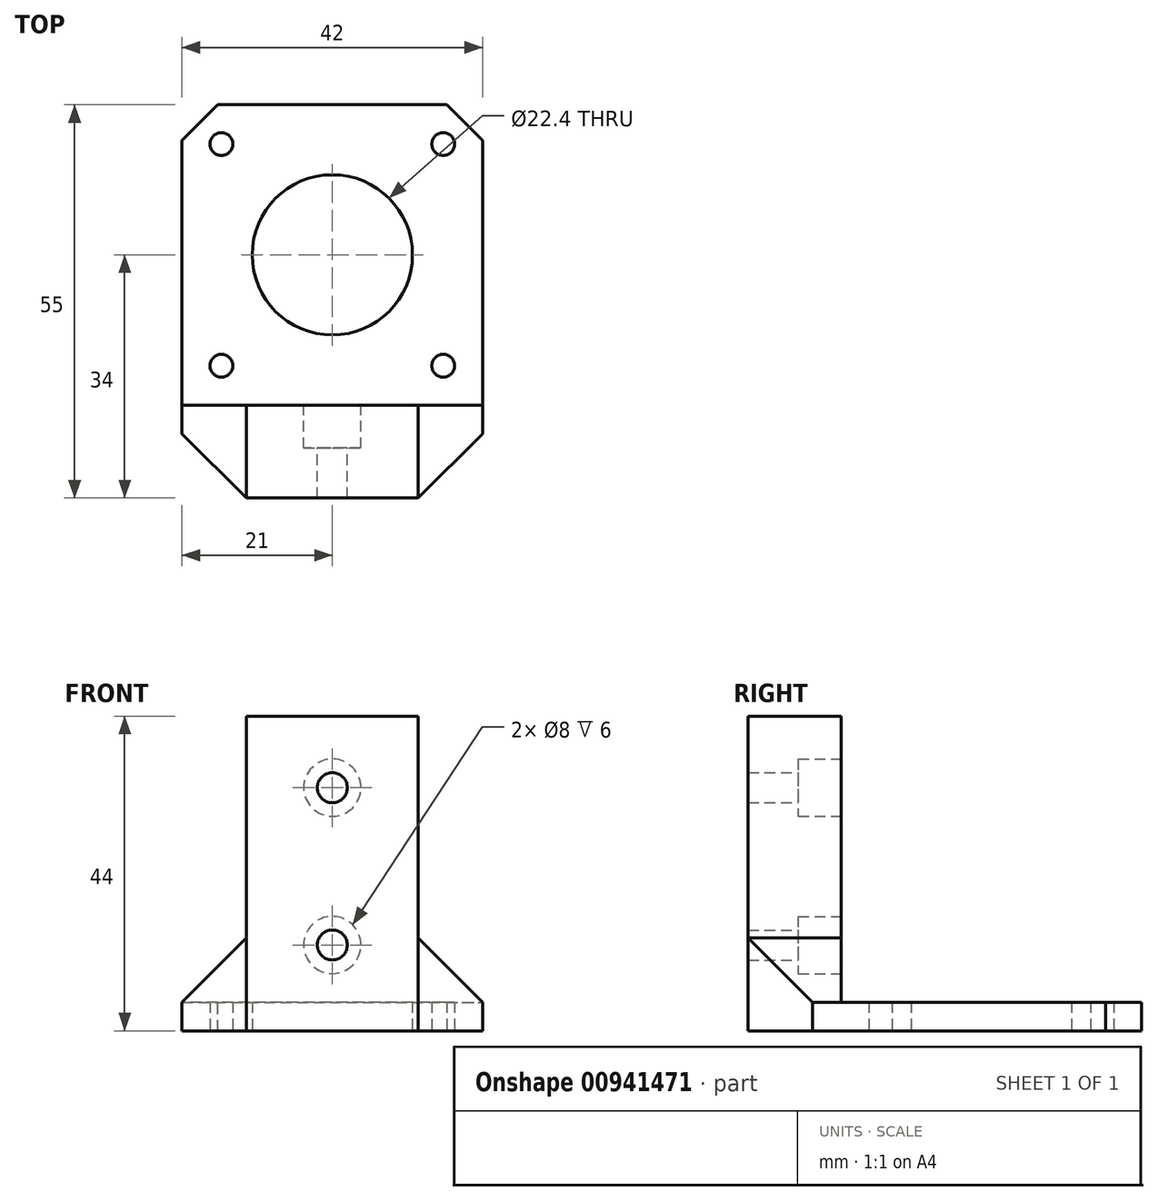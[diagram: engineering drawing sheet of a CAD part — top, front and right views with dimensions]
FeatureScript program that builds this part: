
annotation { "Feature Type Name" : "Feature", "Feature Type Description" : "" }
export const myFeature = defineFeature(function(context is Context, id is Id, definition is map)
    precondition{}
    {
        {
            var Q0;
            Q0=qCreatedBy(makeId("Top.planeOp"),FACE);
            var sketch = newSketch(context, id + "F0", { "sketchPlane" : qUnion([Q0])});
            skLineSegment(sketch, "E0.bottom", {"start": v(21, -21) * mm, "end": v(-21, -21) * mm});
            skLineSegment(sketch, "E0.top", {"start": v(21, 21) * mm, "end": v(-21, 21) * mm});
            skLineSegment(sketch, "E0.left", {"start": v(21, -21) * mm, "end": v(21, 21) * mm});
            skLineSegment(sketch, "E0.right", {"start": v(-21, -21) * mm, "end": v(-21, 21) * mm});
            skPoint(sketch, "E0.middle", {"position": v(0, 0) * mm});
            skLineSegment(sketch, "E1.bottom", {"start": v(-12, -21) * mm, "end": v(12, -21) * mm});
            skLineSegment(sketch, "E1.top", {"start": v(-12, -34) * mm, "end": v(12, -34) * mm});
            skLineSegment(sketch, "E1.left", {"start": v(-12, -21) * mm, "end": v(-12, -34) * mm});
            skLineSegment(sketch, "E1.right", {"start": v(12, -21) * mm, "end": v(12, -34) * mm});
            skCircle(sketch, "E2", {"center": v(0, 0) * mm, "radius": 11.2 * mm});
            skCircle(sketch, "E3", {"center": v(-15.5, 15.5) * mm, "radius": 1.6 * mm});
            skCircle(sketch, "E4", {"center": v(15.5, 15.5) * mm, "radius": 1.6 * mm});
            skCircle(sketch, "E5", {"center": v(15.5, -15.5) * mm, "radius": 1.6 * mm});
            skCircle(sketch, "E6", {"center": v(-15.5, -15.5) * mm, "radius": 1.6 * mm});
            skSolve(sketch);
        }
        {
            var Q0;
            Q0=makeQuery(id+"F0.imprint","IMPRINT",FACE,{"disambiguationData":[TD([[makeQuery(id+"F0.imprint","IMPRINT",EDGE,{"derivedFrom":sQuery(id+"F0.wireOp",EDGE,"E0.top")}),1.0]])]});
            var Q1;
            Q1=makeQuery(id+"F0.imprint","IMPRINT",FACE,{"disambiguationData":[TD([[makeQuery(id+"F0.imprint","IMPRINT",EDGE,{"derivedFrom":sQuery(id+"F0.wireOp",EDGE,"E1.top")}),1.0]])]});
            extrude(context, id + "F1", {"entities" : qUnion([Q0, Q1]), "depth" : 4 * mm, "offsetDistance" : 25 * mm});
        }
        {
            var Q0;
            Q0=makeQuery(id+"F1.opExtrude","CAP_FACE",FACE,{"disambiguationData":[OSD([sQuery(id+"F0.wireOp",EDGE,"E0.bottom"),sQuery(id+"F0.wireOp",EDGE,"E0.top"),sQuery(id+"F0.wireOp",EDGE,"E0.left"),sQuery(id+"F0.wireOp",EDGE,"E0.right"),sQuery(id+"F0.wireOp",EDGE,"E1.top"),sQuery(id+"F0.wireOp",EDGE,"E1.left"),sQuery(id+"F0.wireOp",EDGE,"E1.right"),sQuery(id+"F0.wireOp",EDGE,"E2"),sQuery(id+"F0.wireOp",EDGE,"E3"),sQuery(id+"F0.wireOp",EDGE,"E4"),sQuery(id+"F0.wireOp",EDGE,"E5"),sQuery(id+"F0.wireOp",EDGE,"E6")])],"isStart":false});
            var sketch = newSketch(context, id + "F2", { "sketchPlane" : qUnion([Q0])});
            skLineSegment(sketch, "E7.bottom", {"start": v(-12, -34) * mm, "end": v(12, -34) * mm});
            skLineSegment(sketch, "E7.top", {"start": v(-12, -21) * mm, "end": v(12, -21) * mm});
            skLineSegment(sketch, "E7.left", {"start": v(-12, -34) * mm, "end": v(-12, -21) * mm});
            skLineSegment(sketch, "E7.right", {"start": v(12, -34) * mm, "end": v(12, -21) * mm});
            skSolve(sketch);
        }
        {
            var Q0;
            Q0=makeQuery(id+"F2.imprint","IMPRINT",FACE,{"disambiguationData":[TD([[makeQuery(id+"F2.imprint","IMPRINT",EDGE,{"derivedFrom":sQuery(id+"F2.wireOp",EDGE,"E7.bottom")}),1.0]])]});
            extrude(context, id + "F3", {"entities" : qUnion([Q0]), "operationType" : NewBodyOperationType.ADD, "depth" : 40 * mm, "offsetDistance" : 25 * mm});
        }
        {
            var Q0;
            Q0=makeQuery(id+"F1.opExtrude","SWEPT_EDGE",EDGE,{"disambiguationData":[OSD([sQuery(id+"F0.wireOp",EDGE,"E0.bottom"),sQuery(id+"F0.wireOp",EDGE,"E1.right")])]});
            var Q1;
            Q1=makeQuery(id+"F1.opExtrude","SWEPT_EDGE",EDGE,{"disambiguationData":[OSD([sQuery(id+"F0.wireOp",EDGE,"E0.bottom"),sQuery(id+"F0.wireOp",EDGE,"E1.left")])]});
            chamfer(context, id + "F4", {"entities" : qUnion([Q0, Q1]), "width" : 13 * mm, "tangentPropagation" : true});
        }
        {
            var Q0;
            {var subQ0=sQuery(id+"F0.wireOp",EDGE,"E0.bottom");Q0=makeQuery(id+"F4.opChamfer","TWEAK_EDGE",EDGE,{"derivedFrom":[makeQuery(id+"F3.boolean.opBoolean","MERGE",VERTEX,{"derivedFrom":[makeQuery(id+"F1.opExtrude","CAP_VERTEX",VERTEX,{"disambiguationData":[OSD([subQ0,sQuery(id+"F0.wireOp",EDGE,"E1.right")])],"isStart":false}),makeQuery(id+"F3.opExtrude","CAP_VERTEX",VERTEX,{"disambiguationData":[OSD([subQ0,sQuery(id+"F2.wireOp",EDGE,"E7.top"),sQuery(id+"F2.wireOp",EDGE,"E7.right")])],"isStart":true})]})]});}
            var Q1;
            {var subQ0=sQuery(id+"F0.wireOp",EDGE,"E0.bottom");Q1=makeQuery(id+"F4.opChamfer","TWEAK_EDGE",EDGE,{"derivedFrom":[makeQuery(id+"F3.boolean.opBoolean","MERGE",VERTEX,{"derivedFrom":[makeQuery(id+"F1.opExtrude","CAP_VERTEX",VERTEX,{"disambiguationData":[OSD([subQ0,sQuery(id+"F0.wireOp",EDGE,"E1.left")])],"isStart":false}),makeQuery(id+"F3.opExtrude","CAP_VERTEX",VERTEX,{"disambiguationData":[OSD([subQ0,sQuery(id+"F2.wireOp",EDGE,"E7.top"),sQuery(id+"F2.wireOp",EDGE,"E7.left")])],"isStart":true})]})]});}
            chamfer(context, id + "F5", {"entities" : qUnion([Q0, Q1]), "width" : 9 * mm, "tangentPropagation" : true});
        }
        {
            var Q0;
            Q0=makeQuery(id+"F3.opExtrude","SWEPT_FACE",FACE,{"disambiguationData":[OSD([sQuery(id+"F2.wireOp",EDGE,"E7.top")])]});
            var sketch = newSketch(context, id + "F6", { "sketchPlane" : qUnion([Q0])});
            skCircle(sketch, "E8", {"center": v(0, 34) * mm, "radius": 2.1 * mm});
            skCircle(sketch, "E9", {"center": v(0, 12) * mm, "radius": 2.1 * mm});
            skCircle(sketch, "E10", {"center": v(0, 34) * mm, "radius": 4 * mm});
            skCircle(sketch, "E11", {"center": v(0, 12) * mm, "radius": 4 * mm});
            skSolve(sketch);
        }
        {
            var Q0;
            Q0=makeQuery(id+"F6.imprint","IMPRINT",FACE,{"disambiguationData":[TD([[makeQuery(id+"F6.imprint","IMPRINT",EDGE,{"derivedFrom":sQuery(id+"F6.wireOp",EDGE,"E8")}),1.0]])]});
            var Q1;
            Q1=makeQuery(id+"F6.imprint","IMPRINT",FACE,{"disambiguationData":[TD([[makeQuery(id+"F6.imprint","IMPRINT",EDGE,{"derivedFrom":sQuery(id+"F6.wireOp",EDGE,"E9")}),1.0]])]});
            extrude(context, id + "F7", {"entities" : qUnion([Q0, Q1]), "operationType" : NewBodyOperationType.REMOVE, "oppositeDirection" : true, "depth" : 25 * mm, "offsetDistance" : 25 * mm});
        }
        {
            var Q0;
            Q0=makeQuery(id+"F6.imprint","IMPRINT",FACE,{"disambiguationData":[TD([[makeQuery(id+"F6.imprint","IMPRINT",EDGE,{"derivedFrom":sQuery(id+"F6.wireOp",EDGE,"E8")}),-1.0]])]});
            var Q1;
            Q1=makeQuery(id+"F6.imprint","IMPRINT",FACE,{"disambiguationData":[TD([[makeQuery(id+"F6.imprint","IMPRINT",EDGE,{"derivedFrom":sQuery(id+"F6.wireOp",EDGE,"E9")}),-1.0]])]});
            extrude(context, id + "F8", {"entities" : qUnion([Q0, Q1]), "operationType" : NewBodyOperationType.REMOVE, "oppositeDirection" : true, "depth" : 6 * mm, "offsetDistance" : 25 * mm});
        }
        {
            var Q0;
            Q0=makeQuery(id+"F1.opExtrude","SWEPT_EDGE",EDGE,{"disambiguationData":[OSD([sQuery(id+"F0.wireOp",EDGE,"E0.top"),sQuery(id+"F0.wireOp",EDGE,"E0.left")])]});
            var Q1;
            Q1=makeQuery(id+"F1.opExtrude","SWEPT_EDGE",EDGE,{"disambiguationData":[OSD([sQuery(id+"F0.wireOp",EDGE,"E0.top"),sQuery(id+"F0.wireOp",EDGE,"E0.right")])]});
            chamfer(context, id + "F9", {"entities" : qUnion([Q0, Q1]), "width" : 5 * mm, "tangentPropagation" : true});
        }
    });
